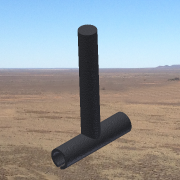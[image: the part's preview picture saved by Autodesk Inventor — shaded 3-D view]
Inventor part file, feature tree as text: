
AUTODESK INVENTOR PART (.ipt)
format: ipt  version: 2014 SP1 (Build 180222100, 222)  size: 155,136 bytes
history: native  units: in
note: dims shown in document units (in); Inventor stores cm internally (conversion verified against a paired STEP export)
features: sketch x4, extrude x3, plane x1
ambient origin geometry x8: Origin, YZ Plane, XZ Plane, XY Plane, X Axis, Y Axis, Z Axis, Center Point
bodies: Solid1 (feature_tree)
feature tree (8):
  extrude  "Extrusion1"  Depth=0.1in
  sketch  "Sketch2"  dims[d2=3.0in d3=0.0in d4=0.65in]
  plane  "Work Plane1"
  extrude  "Extrusion2"  Depth=3.0in
  extrude  "Extrusion3"  Depth=4.0in TaperAngle=0.0deg
  sketch  "Sketch1"  dims[d0=0.75in d1=0.1in]
  sketch  "Sketch3"  dims[d5=4.0in d6=0.25in d7=0.0in d8=0.0in d9=4.0in d10=0.0in]
  sketch  "Sketch4"
